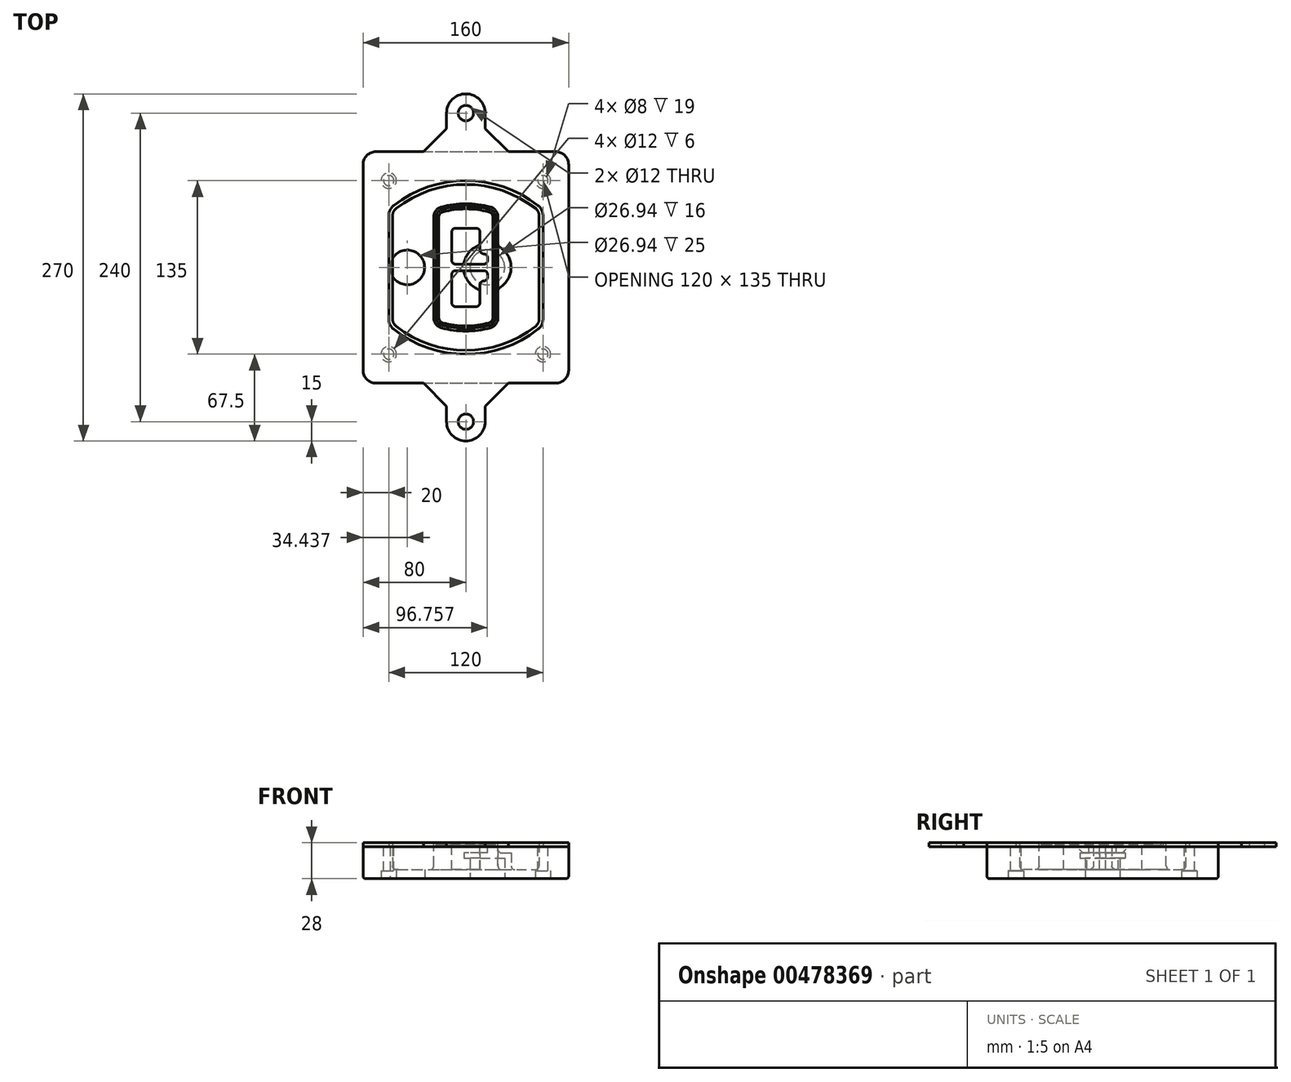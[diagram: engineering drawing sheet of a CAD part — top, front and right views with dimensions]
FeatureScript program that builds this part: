
annotation { "Feature Type Name" : "Feature", "Feature Type Description" : "" }
export const myFeature = defineFeature(function(context is Context, id is Id, definition is map)
    precondition{}
    {
        {
            var Q0;
            Q0=qCreatedBy(makeId("Top.planeOp"),FACE);
            var sketch = newSketch(context, id + "F0", { "sketchPlane" : qUnion([Q0])});
            skPoint(sketch, "E0.rect.middle", {"position": v(0, 0) * mm});
            skLineSegment(sketch, "E1.bottom", {"start": v(-70, -90) * mm, "end": v(70, -90) * mm});
            skLineSegment(sketch, "E1.top", {"start": v(-70, 90) * mm, "end": v(70, 90) * mm});
            skLineSegment(sketch, "E1.left", {"start": v(-80, -80) * mm, "end": v(-80, 80) * mm});
            skLineSegment(sketch, "E1.right", {"start": v(80, -80) * mm, "end": v(80, 80) * mm});
            skLineSegment(sketch, "E2", {"start": v(-80, 90) * mm, "end": v(80, -90) * mm, "construction": true});
            skLineSegment(sketch, "E3", {"start": v(80, 90) * mm, "end": v(-80, -90) * mm, "construction": true});
            skCircle(sketch, "E4", {"center": v(-60, 67.5) * mm, "radius": 4 * mm});
            skCircle(sketch, "E5", {"center": v(60, 67.5) * mm, "radius": 4 * mm});
            skCircle(sketch, "E6", {"center": v(60, -67.5) * mm, "radius": 4 * mm});
            skCircle(sketch, "E7", {"center": v(-60, -67.5) * mm, "radius": 4 * mm});
            skLineSegment(sketch, "E8", {"start": v(-60, 67.5) * mm, "end": v(60, 67.5) * mm, "construction": true});
            skLineSegment(sketch, "E9", {"start": v(60, 67.5) * mm, "end": v(60, -67.5) * mm, "construction": true});
            skLineSegment(sketch, "E10", {"start": v(60, -67.5) * mm, "end": v(-60, -67.5) * mm, "construction": true});
            skLineSegment(sketch, "E11", {"start": v(-60, -67.5) * mm, "end": v(-60, 67.5) * mm, "construction": true});
            skLineSegment(sketch, "E12", {"start": v(-60, 40.3) * mm, "end": v(-60, -40.3) * mm});
            skLineSegment(sketch, "E13", {"start": v(60, 40.3) * mm, "end": v(60, -40.3) * mm});
            skArc(sketch, "E14", {"start": v(56.15, 48.18) * mm, "mid": v(0, 67.5) * mm, "end": v(-56.15, 48.18) * mm});
            skArc(sketch, "E15", {"start": v(-56.15, -48.18) * mm, "mid": v(0, -67.5) * mm, "end": v(56.15, -48.18) * mm});
            skLineSegment(sketch, "E16", {"start": v(-60, 0) * mm, "end": v(60, 0) * mm, "construction": true});
            skPoint(sketch, "E17.visualSharp", {"position": v(-60, -45) * mm});
            skArc(sketch, "E17.filletArc", {"start": v(-60, -40.3) * mm, "mid": v(-58.99, -44.68) * mm, "end": v(-56.15, -48.18) * mm});
            skPoint(sketch, "E18.visualSharp", {"position": v(-60, 45) * mm});
            skArc(sketch, "E18.filletArc", {"start": v(-56.15, 48.18) * mm, "mid": v(-58.99, 44.68) * mm, "end": v(-60, 40.3) * mm});
            skPoint(sketch, "E19.visualSharp", {"position": v(60, 45) * mm});
            skArc(sketch, "E19.filletArc", {"start": v(60, 40.3) * mm, "mid": v(58.99, 44.68) * mm, "end": v(56.15, 48.18) * mm});
            skPoint(sketch, "E20.visualSharp", {"position": v(60, -45) * mm});
            skArc(sketch, "E20.filletArc", {"start": v(56.15, -48.18) * mm, "mid": v(58.99, -44.68) * mm, "end": v(60, -40.3) * mm});
            skPoint(sketch, "E21.visualSharp", {"position": v(-80, 90) * mm});
            skArc(sketch, "E21.filletArc", {"start": v(-70, 90) * mm, "mid": v(-77.07, 87.07) * mm, "end": v(-80, 80) * mm});
            skPoint(sketch, "E22.visualSharp", {"position": v(80, 90) * mm});
            skArc(sketch, "E22.filletArc", {"start": v(80, 80) * mm, "mid": v(77.07, 87.07) * mm, "end": v(70, 90) * mm});
            skPoint(sketch, "E23.visualSharp", {"position": v(80, -90) * mm});
            skArc(sketch, "E23.filletArc", {"start": v(70, -90) * mm, "mid": v(77.07, -87.07) * mm, "end": v(80, -80) * mm});
            skPoint(sketch, "E24.visualSharp", {"position": v(-80, -90) * mm});
            skArc(sketch, "E24.filletArc", {"start": v(-80, -80) * mm, "mid": v(-77.07, -87.07) * mm, "end": v(-70, -90) * mm});
            skArc(sketch, "E25.0", {"start": v(57, 40.3) * mm, "mid": v(56.3, 43.36) * mm, "end": v(54.3, 45.81) * mm});
            skLineSegment(sketch, "E25.1", {"start": v(57, 40.3) * mm, "end": v(57, -40.3) * mm});
            skArc(sketch, "E25.2", {"start": v(54.3, -45.81) * mm, "mid": v(56.3, -43.36) * mm, "end": v(57, -40.3) * mm});
            skArc(sketch, "E25.3", {"start": v(-54.3, -45.81) * mm, "mid": v(0, -64.5) * mm, "end": v(54.3, -45.81) * mm});
            skArc(sketch, "E25.4", {"start": v(-57, -40.3) * mm, "mid": v(-56.3, -43.36) * mm, "end": v(-54.3, -45.81) * mm});
            skArc(sketch, "E25.5", {"start": v(54.3, 45.81) * mm, "mid": v(0, 64.5) * mm, "end": v(-54.3, 45.81) * mm});
            skLineSegment(sketch, "E25.6", {"start": v(-57, 40.3) * mm, "end": v(-57, -40.3) * mm});
            skArc(sketch, "E25.7", {"start": v(-54.3, 45.81) * mm, "mid": v(-56.3, 43.36) * mm, "end": v(-57, 40.3) * mm});
            skArc(sketch, "E26.0", {"start": v(-58.62, 51.33) * mm, "mid": v(-62.58, 46.43) * mm, "end": v(-64, 40.3) * mm});
            skArc(sketch, "E26.1", {"start": v(58.62, 51.33) * mm, "mid": v(0, 71.5) * mm, "end": v(-58.62, 51.33) * mm});
            skArc(sketch, "E26.2", {"start": v(64, 40.3) * mm, "mid": v(62.58, 46.43) * mm, "end": v(58.62, 51.33) * mm});
            skLineSegment(sketch, "E26.3", {"start": v(64, 40.3) * mm, "end": v(64, -40.3) * mm});
            skArc(sketch, "E26.4", {"start": v(58.62, -51.33) * mm, "mid": v(62.58, -46.43) * mm, "end": v(64, -40.3) * mm});
            skLineSegment(sketch, "E26.5", {"start": v(-64, 40.3) * mm, "end": v(-64, -40.3) * mm});
            skArc(sketch, "E26.6", {"start": v(-58.62, -51.33) * mm, "mid": v(0, -71.5) * mm, "end": v(58.62, -51.33) * mm});
            skArc(sketch, "E26.7", {"start": v(-64, -40.3) * mm, "mid": v(-62.58, -46.43) * mm, "end": v(-58.62, -51.33) * mm});
            skSolve(sketch);
        }
        {
            var Q0;
            Q0=makeQuery(id+"F0.imprint","IMPRINT",FACE,{"disambiguationData":[TD([[makeQuery(id+"F0.imprint","IMPRINT",EDGE,{"derivedFrom":sQuery(id+"F0.wireOp",EDGE,"E1.bottom")}),1.0]])]});
            var Q1;
            Q1=makeQuery(id+"F0.imprint","IMPRINT",FACE,{"disambiguationData":[TD([[makeQuery(id+"F0.imprint","IMPRINT",EDGE,{"derivedFrom":sQuery(id+"F0.wireOp",EDGE,"E12")}),1.0]])]});
            var Q2;
            Q2=makeQuery(id+"F0.imprint","IMPRINT",FACE,{"disambiguationData":[TD([[makeQuery(id+"F0.imprint","IMPRINT",EDGE,{"derivedFrom":sQuery(id+"F0.wireOp",EDGE,"E25.0")}),1.0]])]});
            var Q3;
            Q3=makeQuery(id+"F0.imprint","IMPRINT",FACE,{"disambiguationData":[TD([[makeQuery(id+"F0.imprint","IMPRINT",EDGE,{"derivedFrom":sQuery(id+"F0.wireOp",EDGE,"E12")}),-1.0]])]});
            extrude(context, id + "F1", {"entities" : qUnion([Q0, Q1, Q2, Q3]), "oppositeDirection" : true, "depth" : 25 * mm});
        }
        {
            var Q0;
            Q0=makeQuery(id+"F0.imprint","IMPRINT",FACE,{"disambiguationData":[TD([[makeQuery(id+"F0.imprint","IMPRINT",EDGE,{"derivedFrom":sQuery(id+"F0.wireOp",EDGE,"E12")}),1.0]])]});
            extrude(context, id + "F2", {"entities" : qUnion([Q0]), "operationType" : NewBodyOperationType.ADD, "depth" : 3 * mm});
        }
        {
            var Q0;
            Q0=makeQuery(id+"F0.imprint","IMPRINT",FACE,{"disambiguationData":[TD([[makeQuery(id+"F0.imprint","IMPRINT",EDGE,{"derivedFrom":sQuery(id+"F0.wireOp",EDGE,"E25.0")}),1.0]])]});
            extrude(context, id + "F3", {"entities" : qUnion([Q0]), "operationType" : NewBodyOperationType.REMOVE, "oppositeDirection" : true, "depth" : 18 * mm});
        }
        {
            var Q0;
            Q0=makeQuery(id+"F2.opExtrude","CAP_FACE",FACE,{"disambiguationData":[OSD([sQuery(id+"F0.wireOp",EDGE,"E12"),sQuery(id+"F0.wireOp",EDGE,"E13"),sQuery(id+"F0.wireOp",EDGE,"E14"),sQuery(id+"F0.wireOp",EDGE,"E15"),sQuery(id+"F0.wireOp",EDGE,"E17.filletArc"),sQuery(id+"F0.wireOp",EDGE,"E18.filletArc"),sQuery(id+"F0.wireOp",EDGE,"E19.filletArc"),sQuery(id+"F0.wireOp",EDGE,"E20.filletArc"),sQuery(id+"F0.wireOp",EDGE,"E25.0"),sQuery(id+"F0.wireOp",EDGE,"E25.1"),sQuery(id+"F0.wireOp",EDGE,"E25.2"),sQuery(id+"F0.wireOp",EDGE,"E25.3"),sQuery(id+"F0.wireOp",EDGE,"E25.4"),sQuery(id+"F0.wireOp",EDGE,"E25.5"),sQuery(id+"F0.wireOp",EDGE,"E25.6"),sQuery(id+"F0.wireOp",EDGE,"E25.7")])],"isStart":false});
            var sketch = newSketch(context, id + "F4", { "sketchPlane" : qUnion([Q0])});
            skArc(sketch, "E27.0", {"start": v(-19.08, -46.97) * mm, "mid": v(0, -49.5) * mm, "end": v(19.08, -46.97) * mm});
            skArc(sketch, "E28.0", {"start": v(19.08, 46.97) * mm, "mid": v(0, 49.5) * mm, "end": v(-19.08, 46.97) * mm});
            skLineSegment(sketch, "E29", {"start": v(-25, 39.25) * mm, "end": v(-25, -39.25) * mm});
            skLineSegment(sketch, "E30", {"start": v(25, 39.25) * mm, "end": v(25, -39.25) * mm});
            skLineSegment(sketch, "E31", {"start": v(-25, 45.1) * mm, "end": v(25, 45.1) * mm, "construction": true});
            skLineSegment(sketch, "E32", {"start": v(-25, -45.1) * mm, "end": v(25, -45.1) * mm, "construction": true});
            skPoint(sketch, "E33.visualSharp", {"position": v(-25, 45.1) * mm});
            skArc(sketch, "E33.filletArc", {"start": v(-19.08, 46.97) * mm, "mid": v(-23.35, 44.11) * mm, "end": v(-25, 39.25) * mm});
            skPoint(sketch, "E34.visualSharp", {"position": v(25, 45.1) * mm});
            skArc(sketch, "E34.filletArc", {"start": v(25, 39.25) * mm, "mid": v(23.35, 44.11) * mm, "end": v(19.08, 46.97) * mm});
            skPoint(sketch, "E35.visualSharp", {"position": v(25, -45.1) * mm});
            skArc(sketch, "E35.filletArc", {"start": v(19.08, -46.97) * mm, "mid": v(23.35, -44.11) * mm, "end": v(25, -39.25) * mm});
            skPoint(sketch, "E36.visualSharp", {"position": v(-25, -45.1) * mm});
            skArc(sketch, "E36.filletArc", {"start": v(-25, -39.25) * mm, "mid": v(-23.35, -44.11) * mm, "end": v(-19.08, -46.97) * mm});
            skArc(sketch, "E37.0", {"start": v(54.3, 45.81) * mm, "mid": v(0, 64.5) * mm, "end": v(-54.3, 45.81) * mm});
            skArc(sketch, "E37.1", {"start": v(-54.3, 45.81) * mm, "mid": v(-56.3, 43.36) * mm, "end": v(-57, 40.3) * mm});
            skLineSegment(sketch, "E37.2", {"start": v(-57, 40.3) * mm, "end": v(-57, -40.3) * mm});
            skArc(sketch, "E37.3", {"start": v(-57, -40.3) * mm, "mid": v(-56.3, -43.36) * mm, "end": v(-54.3, -45.81) * mm});
            skArc(sketch, "E37.4", {"start": v(-54.3, -45.81) * mm, "mid": v(0, -64.5) * mm, "end": v(54.3, -45.81) * mm});
            skArc(sketch, "E37.5", {"start": v(54.3, -45.81) * mm, "mid": v(56.3, -43.36) * mm, "end": v(57, -40.3) * mm});
            skLineSegment(sketch, "E37.6", {"start": v(57, 40.3) * mm, "end": v(57, -40.3) * mm});
            skArc(sketch, "E37.7", {"start": v(57, 40.3) * mm, "mid": v(56.3, 43.36) * mm, "end": v(54.3, 45.81) * mm});
            skLineSegment(sketch, "E38.0", {"start": v(23, 39.25) * mm, "end": v(23, -39.25) * mm});
            skArc(sketch, "E38.1", {"start": v(18.56, -45.04) * mm, "mid": v(21.76, -42.9) * mm, "end": v(23, -39.25) * mm});
            skArc(sketch, "E38.2", {"start": v(-18.56, -45.04) * mm, "mid": v(0, -47.5) * mm, "end": v(18.56, -45.04) * mm});
            skArc(sketch, "E38.3", {"start": v(-23, -39.25) * mm, "mid": v(-21.76, -42.9) * mm, "end": v(-18.56, -45.04) * mm});
            skLineSegment(sketch, "E38.4", {"start": v(-23, 39.25) * mm, "end": v(-23, -39.25) * mm});
            skArc(sketch, "E38.5", {"start": v(23, 39.25) * mm, "mid": v(21.76, 42.9) * mm, "end": v(18.56, 45.04) * mm});
            skArc(sketch, "E38.6", {"start": v(-18.56, 45.04) * mm, "mid": v(-21.76, 42.9) * mm, "end": v(-23, 39.25) * mm});
            skArc(sketch, "E38.7", {"start": v(18.56, 45.04) * mm, "mid": v(0, 47.5) * mm, "end": v(-18.56, 45.04) * mm});
            skArc(sketch, "E39.0", {"start": v(21, 39.25) * mm, "mid": v(20.18, 41.68) * mm, "end": v(18.04, 43.1) * mm});
            skLineSegment(sketch, "E39.1", {"start": v(21, 39.25) * mm, "end": v(21, -39.25) * mm});
            skArc(sketch, "E39.2", {"start": v(18.04, -43.1) * mm, "mid": v(20.18, -41.68) * mm, "end": v(21, -39.25) * mm});
            skArc(sketch, "E39.3", {"start": v(-18.04, -43.1) * mm, "mid": v(0, -45.5) * mm, "end": v(18.04, -43.1) * mm});
            skArc(sketch, "E39.4", {"start": v(-21, -39.25) * mm, "mid": v(-20.18, -41.68) * mm, "end": v(-18.04, -43.1) * mm});
            skArc(sketch, "E39.5", {"start": v(18.04, 43.1) * mm, "mid": v(0, 45.5) * mm, "end": v(-18.04, 43.1) * mm});
            skLineSegment(sketch, "E39.6", {"start": v(-21, 39.25) * mm, "end": v(-21, -39.25) * mm});
            skArc(sketch, "E39.7", {"start": v(-18.04, 43.1) * mm, "mid": v(-20.18, 41.68) * mm, "end": v(-21, 39.25) * mm});
            skLineSegment(sketch, "E40", {"start": v(-25, 0) * mm, "end": v(25, 0) * mm, "construction": true});
            skLineSegment(sketch, "E41", {"start": v(-11, 5.5) * mm, "end": v(-11, 27.5) * mm});
            skLineSegment(sketch, "E42", {"start": v(-8, 30.5) * mm, "end": v(8, 30.5) * mm});
            skLineSegment(sketch, "E43", {"start": v(11, 27.5) * mm, "end": v(11, 13.5) * mm});
            skLineSegment(sketch, "E44", {"start": v(14, 10.5) * mm, "end": v(14, 10.5) * mm});
            skLineSegment(sketch, "E45", {"start": v(17, 7.5) * mm, "end": v(17, 5.5) * mm});
            skLineSegment(sketch, "E46", {"start": v(14, 2.5) * mm, "end": v(-8, 2.5) * mm});
            skPoint(sketch, "E47.visualSharp", {"position": v(-11, 30.5) * mm});
            skArc(sketch, "E47.filletArc", {"start": v(-8, 30.5) * mm, "mid": v(-10.12, 29.62) * mm, "end": v(-11, 27.5) * mm});
            skPoint(sketch, "E48.visualSharp", {"position": v(11, 30.5) * mm});
            skArc(sketch, "E48.filletArc", {"start": v(11, 27.5) * mm, "mid": v(10.12, 29.62) * mm, "end": v(8, 30.5) * mm});
            skPoint(sketch, "E49.visualSharp", {"position": v(11, 10.5) * mm});
            skArc(sketch, "E49.filletArc", {"start": v(11, 13.5) * mm, "mid": v(11.88, 11.38) * mm, "end": v(14, 10.5) * mm});
            skPoint(sketch, "E50.visualSharp", {"position": v(17, 10.5) * mm});
            skArc(sketch, "E50.filletArc", {"start": v(17, 7.5) * mm, "mid": v(16.12, 9.62) * mm, "end": v(14, 10.5) * mm});
            skPoint(sketch, "E51.visualSharp", {"position": v(17, 2.5) * mm});
            skArc(sketch, "E51.filletArc", {"start": v(14, 2.5) * mm, "mid": v(16.12, 3.38) * mm, "end": v(17, 5.5) * mm});
            skPoint(sketch, "E52.visualSharp", {"position": v(-11, 2.5) * mm});
            skArc(sketch, "E52.filletArc", {"start": v(-11, 5.5) * mm, "mid": v(-10.12, 3.38) * mm, "end": v(-8, 2.5) * mm});
            skLineSegment(sketch, "E53.0.MirrorCS", {"start": v(14, -2.5) * mm, "end": v(-8, -2.5) * mm});
            skArc(sketch, "E54.0.MirrorCS", {"start": v(-11, -5.5) * mm, "mid": v(-10.12, -3.38) * mm, "end": v(-8, -2.5) * mm});
            skLineSegment(sketch, "E55.0.MirrorCS", {"start": v(-11, -5.5) * mm, "end": v(-11, -27.5) * mm});
            skArc(sketch, "E56.0.MirrorCS", {"start": v(-8, -30.5) * mm, "mid": v(-10.12, -29.62) * mm, "end": v(-11, -27.5) * mm});
            skLineSegment(sketch, "E57.0.MirrorCS", {"start": v(-8, -30.5) * mm, "end": v(8, -30.5) * mm});
            skArc(sketch, "E58.0.MirrorCS", {"start": v(11, -27.5) * mm, "mid": v(10.12, -29.62) * mm, "end": v(8, -30.5) * mm});
            skLineSegment(sketch, "E59.0.MirrorCS", {"start": v(11, -27.5) * mm, "end": v(11, -13.5) * mm});
            skArc(sketch, "E60.0.MirrorCS", {"start": v(11, -13.5) * mm, "mid": v(11.88, -11.38) * mm, "end": v(14, -10.5) * mm});
            skArc(sketch, "E61.0.MirrorCS", {"start": v(17, -7.5) * mm, "mid": v(16.12, -9.62) * mm, "end": v(14, -10.5) * mm});
            skLineSegment(sketch, "E62.0.MirrorCS", {"start": v(17, -7.5) * mm, "end": v(17, -5.5) * mm});
            skArc(sketch, "E63.0.MirrorCS", {"start": v(14, -2.5) * mm, "mid": v(16.12, -3.38) * mm, "end": v(17, -5.5) * mm});
            skSolve(sketch);
        }
        {
            var Q0;
            Q0=makeQuery(id+"F4.imprint","IMPRINT",FACE,{"disambiguationData":[TD([[makeQuery(id+"F4.imprint","IMPRINT",EDGE,{"derivedFrom":sQuery(id+"F4.wireOp",EDGE,"E27.0")}),1.0]])]});
            var Q1;
            Q1=makeQuery(id+"F4.imprint","IMPRINT",FACE,{"disambiguationData":[TD([[makeQuery(id+"F4.imprint","IMPRINT",EDGE,{"derivedFrom":sQuery(id+"F4.wireOp",EDGE,"E38.0")}),-1.0]])]});
            var Q2;
            Q2=makeQuery(id+"F4.imprint","IMPRINT",FACE,{"disambiguationData":[TD([[makeQuery(id+"F4.imprint","IMPRINT",EDGE,{"derivedFrom":sQuery(id+"F4.wireOp",EDGE,"E39.0")}),1.0]])]});
            extrude(context, id + "F5", {"entities" : qUnion([Q0, Q1, Q2]), "operationType" : NewBodyOperationType.ADD, "endBound" : BoundingType.UP_TO_NEXT, "oppositeDirection" : true, "depth" : 25 * mm});
        }
        {
            var Q0;
            Q0=makeQuery(id+"F4.imprint","IMPRINT",FACE,{"disambiguationData":[TD([[makeQuery(id+"F4.imprint","IMPRINT",EDGE,{"derivedFrom":sQuery(id+"F4.wireOp",EDGE,"E38.0")}),-1.0]])]});
            extrude(context, id + "F6", {"entities" : qUnion([Q0]), "operationType" : NewBodyOperationType.REMOVE, "oppositeDirection" : true, "depth" : 2 * mm});
        }
        {
            var Q0;
            Q0=makeQuery(id+"F1.opExtrude","CAP_FACE",FACE,{"disambiguationData":[OSD([sQuery(id+"F0.wireOp",EDGE,"E1.bottom"),sQuery(id+"F0.wireOp",EDGE,"E1.top"),sQuery(id+"F0.wireOp",EDGE,"E1.left"),sQuery(id+"F0.wireOp",EDGE,"E1.right"),sQuery(id+"F0.wireOp",EDGE,"E4"),sQuery(id+"F0.wireOp",EDGE,"E5"),sQuery(id+"F0.wireOp",EDGE,"E6"),sQuery(id+"F0.wireOp",EDGE,"E7"),sQuery(id+"F0.wireOp",EDGE,"E21.filletArc"),sQuery(id+"F0.wireOp",EDGE,"E22.filletArc"),sQuery(id+"F0.wireOp",EDGE,"E23.filletArc"),sQuery(id+"F0.wireOp",EDGE,"E24.filletArc")])],"isStart":false});
            var sketch = newSketch(context, id + "F7", { "sketchPlane" : qUnion([Q0])});
            skCircle(sketch, "E64", {"center": v(16.76, 0) * mm, "radius": 13.47 * mm});
            skCircle(sketch, "E65", {"center": v(-45.56, 0) * mm, "radius": 13.47 * mm});
            skLineSegment(sketch, "E66", {"start": v(80, 0) * mm, "end": v(-80, 0) * mm});
            skCircle(sketch, "E67", {"center": v(16.76, 0) * mm, "radius": 18.47 * mm});
            skCircle(sketch, "E68", {"center": v(60, -67.5) * mm, "radius": 6 * mm});
            skCircle(sketch, "E69", {"center": v(-60, -67.5) * mm, "radius": 6 * mm});
            skCircle(sketch, "E70", {"center": v(-60, 67.5) * mm, "radius": 6 * mm});
            skCircle(sketch, "E71", {"center": v(60, 67.5) * mm, "radius": 6 * mm});
            skSolve(sketch);
        }
        {
            var Q0;
            {var subQ1=sQuery(id+"F7.wireOp",EDGE,"E66");var subQ4=sQuery(id+"F7.wireOp",EDGE,"E64");var subQ6=makeQuery(id+"F7.imprint","INTERSECT",VERTEX,{"disambiguationData":[OD(0.0)],"derivedFrom":[subQ4,subQ1]});Q0=makeQuery(id+"F7.imprint","IMPRINT",FACE,{"disambiguationData":[TD([[makeQuery(id+"F7.imprint","IMPRINT",EDGE,{"disambiguationData":[TD([[subQ6,-1.0]])],"derivedFrom":subQ4}),-1.0]])]});}
            var Q1;
            {var subQ0=sQuery(id+"F7.wireOp",EDGE,"E66");var subQ1=sQuery(id+"F7.wireOp",EDGE,"E64");var subQ3=makeQuery(id+"F7.imprint","INTERSECT",VERTEX,{"disambiguationData":[OD(0.0)],"derivedFrom":[subQ1,subQ0]});Q1=makeQuery(id+"F7.imprint","IMPRINT",FACE,{"disambiguationData":[TD([[makeQuery(id+"F7.imprint","IMPRINT",EDGE,{"disambiguationData":[TD([[subQ3,-1.0]])],"derivedFrom":subQ1}),1.0]])]});}
            var Q2;
            {var subQ0=sQuery(id+"F7.wireOp",EDGE,"E66");var subQ1=sQuery(id+"F7.wireOp",EDGE,"E64");var subQ3=makeQuery(id+"F7.imprint","INTERSECT",VERTEX,{"disambiguationData":[OD(0.0)],"derivedFrom":[subQ1,subQ0]});Q2=makeQuery(id+"F7.imprint","IMPRINT",FACE,{"disambiguationData":[TD([[makeQuery(id+"F7.imprint","IMPRINT",EDGE,{"disambiguationData":[TD([[subQ3,1.0]])],"derivedFrom":subQ1}),1.0]])]});}
            var Q3;
            {var subQ1=sQuery(id+"F7.wireOp",EDGE,"E66");var subQ4=sQuery(id+"F7.wireOp",EDGE,"E64");var subQ6=makeQuery(id+"F7.imprint","INTERSECT",VERTEX,{"disambiguationData":[OD(0.0)],"derivedFrom":[subQ4,subQ1]});Q3=makeQuery(id+"F7.imprint","IMPRINT",FACE,{"disambiguationData":[TD([[makeQuery(id+"F7.imprint","IMPRINT",EDGE,{"disambiguationData":[TD([[subQ6,1.0]])],"derivedFrom":subQ4}),-1.0]])]});}
            extrude(context, id + "F8", {"entities" : qUnion([Q0, Q1, Q2, Q3]), "operationType" : NewBodyOperationType.ADD, "oppositeDirection" : true, "depth" : 20 * mm});
        }
        {
            var Q0;
            {var subQ0=sQuery(id+"F7.wireOp",EDGE,"E66");var subQ1=sQuery(id+"F7.wireOp",EDGE,"E64");var subQ3=makeQuery(id+"F7.imprint","INTERSECT",VERTEX,{"disambiguationData":[OD(0.0)],"derivedFrom":[subQ1,subQ0]});Q0=makeQuery(id+"F7.imprint","IMPRINT",FACE,{"disambiguationData":[TD([[makeQuery(id+"F7.imprint","IMPRINT",EDGE,{"disambiguationData":[TD([[subQ3,-1.0]])],"derivedFrom":subQ1}),1.0]])]});}
            var Q1;
            {var subQ0=sQuery(id+"F7.wireOp",EDGE,"E66");var subQ1=sQuery(id+"F7.wireOp",EDGE,"E64");var subQ3=makeQuery(id+"F7.imprint","INTERSECT",VERTEX,{"disambiguationData":[OD(0.0)],"derivedFrom":[subQ1,subQ0]});Q1=makeQuery(id+"F7.imprint","IMPRINT",FACE,{"disambiguationData":[TD([[makeQuery(id+"F7.imprint","IMPRINT",EDGE,{"disambiguationData":[TD([[subQ3,1.0]])],"derivedFrom":subQ1}),1.0]])]});}
            extrude(context, id + "F9", {"entities" : qUnion([Q0, Q1]), "operationType" : NewBodyOperationType.REMOVE, "oppositeDirection" : true, "depth" : 16 * mm});
        }
        {
            var Q0;
            {var subQ0=sQuery(id+"F7.wireOp",EDGE,"E66");var subQ1=sQuery(id+"F7.wireOp",EDGE,"E65");var subQ3=makeQuery(id+"F7.imprint","INTERSECT",VERTEX,{"disambiguationData":[OD(0.0)],"derivedFrom":[subQ1,subQ0]});Q0=makeQuery(id+"F7.imprint","IMPRINT",FACE,{"disambiguationData":[TD([[makeQuery(id+"F7.imprint","IMPRINT",EDGE,{"disambiguationData":[TD([[subQ3,-1.0]])],"derivedFrom":subQ1}),1.0]])]});}
            var Q1;
            {var subQ0=sQuery(id+"F7.wireOp",EDGE,"E66");var subQ1=sQuery(id+"F7.wireOp",EDGE,"E65");var subQ3=makeQuery(id+"F7.imprint","INTERSECT",VERTEX,{"disambiguationData":[OD(0.0)],"derivedFrom":[subQ1,subQ0]});Q1=makeQuery(id+"F7.imprint","IMPRINT",FACE,{"disambiguationData":[TD([[makeQuery(id+"F7.imprint","IMPRINT",EDGE,{"disambiguationData":[TD([[subQ3,1.0]])],"derivedFrom":subQ1}),1.0]])]});}
            extrude(context, id + "F10", {"entities" : qUnion([Q0, Q1]), "operationType" : NewBodyOperationType.REMOVE, "oppositeDirection" : true, "depth" : 25 * mm});
        }
        {
            var Q0;
            Q0=makeQuery(id+"F7.imprint","IMPRINT",FACE,{"disambiguationData":[TD([[makeQuery(id+"F7.imprint","IMPRINT",EDGE,{"derivedFrom":sQuery(id+"F7.wireOp",EDGE,"E68")}),1.0]])]});
            var Q1;
            Q1=makeQuery(id+"F7.imprint","IMPRINT",FACE,{"disambiguationData":[TD([[makeQuery(id+"F7.imprint","IMPRINT",EDGE,{"derivedFrom":makeQuery(id+"F1.opExtrude","CAP_EDGE",EDGE,{"disambiguationData":[OSD([sQuery(id+"F0.wireOp",EDGE,"E5")])],"isStart":false})}),-1.0]])]});
            var Q2;
            Q2=makeQuery(id+"F7.imprint","IMPRINT",FACE,{"disambiguationData":[TD([[makeQuery(id+"F7.imprint","IMPRINT",EDGE,{"derivedFrom":sQuery(id+"F7.wireOp",EDGE,"E69")}),1.0]])]});
            var Q3;
            Q3=makeQuery(id+"F7.imprint","IMPRINT",FACE,{"disambiguationData":[TD([[makeQuery(id+"F7.imprint","IMPRINT",EDGE,{"derivedFrom":makeQuery(id+"F1.opExtrude","CAP_EDGE",EDGE,{"disambiguationData":[OSD([sQuery(id+"F0.wireOp",EDGE,"E4")])],"isStart":false})}),-1.0]])]});
            var Q4;
            Q4=makeQuery(id+"F7.imprint","IMPRINT",FACE,{"disambiguationData":[TD([[makeQuery(id+"F7.imprint","IMPRINT",EDGE,{"derivedFrom":sQuery(id+"F7.wireOp",EDGE,"E70")}),1.0]])]});
            var Q5;
            Q5=makeQuery(id+"F7.imprint","IMPRINT",FACE,{"disambiguationData":[TD([[makeQuery(id+"F7.imprint","IMPRINT",EDGE,{"derivedFrom":makeQuery(id+"F1.opExtrude","CAP_EDGE",EDGE,{"disambiguationData":[OSD([sQuery(id+"F0.wireOp",EDGE,"E7")])],"isStart":false})}),-1.0]])]});
            var Q6;
            Q6=makeQuery(id+"F7.imprint","IMPRINT",FACE,{"disambiguationData":[TD([[makeQuery(id+"F7.imprint","IMPRINT",EDGE,{"derivedFrom":sQuery(id+"F7.wireOp",EDGE,"E71")}),1.0]])]});
            var Q7;
            Q7=makeQuery(id+"F7.imprint","IMPRINT",FACE,{"disambiguationData":[TD([[makeQuery(id+"F7.imprint","IMPRINT",EDGE,{"derivedFrom":makeQuery(id+"F1.opExtrude","CAP_EDGE",EDGE,{"disambiguationData":[OSD([sQuery(id+"F0.wireOp",EDGE,"E6")])],"isStart":false})}),-1.0]])]});
            extrude(context, id + "F11", {"entities" : qUnion([Q0, Q1, Q2, Q3, Q4, Q5, Q6, Q7]), "operationType" : NewBodyOperationType.REMOVE, "oppositeDirection" : true, "depth" : 6 * mm});
        }
        {
            var Q0;
            Q0=makeQuery(id+"F9.boolean.opBoolean","COPY",FACE,{"derivedFrom":makeQuery(id+"F9.opExtrude","CAP_FACE",FACE,{"disambiguationData":[OSD([sQuery(id+"F7.wireOp",EDGE,"E64")])],"isStart":false})});
            var sketch = newSketch(context, id + "F12", { "sketchPlane" : qUnion([Q0])});
            skArc(sketch, "E72.0", {"start": v(11, 17.55) * mm, "mid": v(2.57, 11.82) * mm, "end": v(-1.54, 2.5) * mm});
            skArc(sketch, "E72.1", {"start": v(-1.54, -2.5) * mm, "mid": v(2.57, -11.82) * mm, "end": v(11, -17.55) * mm});
            skLineSegment(sketch, "E73", {"start": v(-1.54, -2.5) * mm, "end": v(14, -2.5) * mm});
            skLineSegment(sketch, "E74.0", {"start": v(14, 2.5) * mm, "end": v(-1.54, 2.5) * mm});
            skArc(sketch, "E74.1", {"start": v(14, 2.5) * mm, "mid": v(16.12, 3.38) * mm, "end": v(17, 5.5) * mm});
            skLineSegment(sketch, "E74.2", {"start": v(17, 7.5) * mm, "end": v(17, 5.5) * mm});
            skArc(sketch, "E74.3", {"start": v(17, 7.5) * mm, "mid": v(16.12, 9.62) * mm, "end": v(14, 10.5) * mm});
            skArc(sketch, "E74.4", {"start": v(11, 13.5) * mm, "mid": v(11.88, 11.38) * mm, "end": v(14, 10.5) * mm});
            skLineSegment(sketch, "E74.5", {"start": v(11, 17.55) * mm, "end": v(11, 13.5) * mm});
            skLineSegment(sketch, "E74.7", {"start": v(14, -2.5) * mm, "end": v(-1.54, -2.5) * mm});
            skArc(sketch, "E74.8", {"start": v(14, -2.5) * mm, "mid": v(16.12, -3.38) * mm, "end": v(17, -5.5) * mm});
            skLineSegment(sketch, "E74.9", {"start": v(17, -7.5) * mm, "end": v(17, -5.5) * mm});
            skArc(sketch, "E74.10", {"start": v(17, -7.5) * mm, "mid": v(16.12, -9.62) * mm, "end": v(14, -10.5) * mm});
            skArc(sketch, "E74.11", {"start": v(11, -13.5) * mm, "mid": v(11.88, -11.38) * mm, "end": v(14, -10.5) * mm});
            skLineSegment(sketch, "E74.12", {"start": v(11, -17.55) * mm, "end": v(11, -13.5) * mm});
            skPoint(sketch, "E75.orphan", {"position": v(11, -27.5) * mm});
            skPoint(sketch, "E76.orphan", {"position": v(-8, -2.5) * mm});
            skPoint(sketch, "E77.orphan", {"position": v(-8, 2.5) * mm});
            skPoint(sketch, "E78.orphan", {"position": v(11, 27.5) * mm});
            skSolve(sketch);
        }
        {
            var Q0;
            {var subQ7=sQuery(id+"F12.wireOp",EDGE,"E72.0");var subQ14=sQuery(id+"F12.wireOp",EDGE,"E72.1");var subQ16=sQuery(id+"F12.wireOp",EDGE,"E74.1");var subQ18=sQuery(id+"F12.wireOp",EDGE,"E74.8");Q0=qUnion([makeQuery(id+"F12.imprint","IMPRINT",FACE,{"disambiguationData":[TD([[makeQuery(id+"F12.imprint","IMPRINT",EDGE,{"derivedFrom":subQ7}),1.0]])]}),makeQuery(id+"F12.imprint","IMPRINT",FACE,{"disambiguationData":[TD([[makeQuery(id+"F12.imprint","IMPRINT",EDGE,{"derivedFrom":subQ14}),1.0]])]}),makeQuery(id+"F12.imprint","IMPRINT",FACE,{"disambiguationData":[TD([[makeQuery(id+"F12.imprint","IMPRINT",EDGE,{"derivedFrom":subQ16}),1.0]])]}),makeQuery(id+"F12.imprint","IMPRINT",FACE,{"disambiguationData":[TD([[makeQuery(id+"F12.imprint","IMPRINT",EDGE,{"derivedFrom":subQ18}),-1.0]])]})]);}
            var Q1;
            Q1=makeQuery(id+"F5.boolean.opBoolean","SPLIT",FACE,{"disambiguationData":[TD([makeQuery(id+"F5.opExtrude","SWEPT_FACE",FACE,{"disambiguationData":[OSD([sQuery(id+"F4.wireOp",EDGE,"E41")])]})])],"derivedFrom":makeQuery(id+"F3.boolean.opBoolean","COPY",FACE,{"derivedFrom":makeQuery(id+"F3.opExtrude","CAP_FACE",FACE,{"disambiguationData":[OSD([sQuery(id+"F0.wireOp",EDGE,"E25.0"),sQuery(id+"F0.wireOp",EDGE,"E25.1"),sQuery(id+"F0.wireOp",EDGE,"E25.2"),sQuery(id+"F0.wireOp",EDGE,"E25.3"),sQuery(id+"F0.wireOp",EDGE,"E25.4"),sQuery(id+"F0.wireOp",EDGE,"E25.5"),sQuery(id+"F0.wireOp",EDGE,"E25.6"),sQuery(id+"F0.wireOp",EDGE,"E25.7")])],"isStart":false})})});
            extrude(context, id + "F13", {"entities" : qUnion([Q0]), "operationType" : NewBodyOperationType.REMOVE, "endBound" : BoundingType.UP_TO_SURFACE, "endBoundEntityFace" : qUnion([Q1]), "depth" : 25 * mm});
        }
        {
            var Q0;
            Q0=makeQuery(id+"F3.boolean.opBoolean","COPY",EDGE,{"derivedFrom":makeQuery(id+"F3.opExtrude","CAP_EDGE",EDGE,{"disambiguationData":[OSD([sQuery(id+"F0.wireOp",EDGE,"E25.6")])],"isStart":false})});
            var Q1;
            Q1=makeQuery(id+"F8.boolean.opBoolean","INTERSECT",EDGE,{"derivedFrom":[makeQuery(id+"F5.opExtrude","SWEPT_FACE",FACE,{"disambiguationData":[OSD([sQuery(id+"F4.wireOp",EDGE,"E30")])]}),makeQuery(id+"F8.opExtrude","CAP_FACE",FACE,{"disambiguationData":[OSD([sQuery(id+"F7.wireOp",EDGE,"E67")])],"isStart":false})]});
            var Q2;
            Q2=makeQuery(id+"F8.boolean.opBoolean","INTERSECT",EDGE,{"disambiguationData":[OD(1.0)],"derivedFrom":[makeQuery(id+"F5.opExtrude","SWEPT_FACE",FACE,{"disambiguationData":[OSD([sQuery(id+"F4.wireOp",EDGE,"E30")])]}),makeQuery(id+"F8.opExtrude","SWEPT_FACE",FACE,{"disambiguationData":[OSD([sQuery(id+"F7.wireOp",EDGE,"E67")])]})]});
            var Q3;
            {var subQ0=sQuery(id+"F4.wireOp",EDGE,"E30");Q3=makeQuery(id+"F8.boolean.opBoolean","SPLIT",EDGE,{"disambiguationData":[TD([makeQuery(id+"F5.opExtrude","SWEPT_FACE",FACE,{"disambiguationData":[OSD([sQuery(id+"F4.wireOp",EDGE,"E35.filletArc")])]})])],"derivedFrom":makeQuery(id+"F5.opExtrude","CAP_EDGE",EDGE,{"disambiguationData":[OSD([subQ0])],"isStart":false})});}
            var Q4;
            {var subQ0=sQuery(id+"F0.wireOp",EDGE,"E25.7");var subQ1=sQuery(id+"F0.wireOp",EDGE,"E25.1");var subQ2=sQuery(id+"F0.wireOp",EDGE,"E25.6");var subQ3=sQuery(id+"F0.wireOp",EDGE,"E25.5");var subQ4=sQuery(id+"F0.wireOp",EDGE,"E25.4");var subQ5=sQuery(id+"F0.wireOp",EDGE,"E25.0");var subQ6=sQuery(id+"F0.wireOp",EDGE,"E25.2");var subQ7=sQuery(id+"F0.wireOp",EDGE,"E25.3");Q4=makeQuery(id+"F8.boolean.opBoolean","INTERSECT",EDGE,{"derivedFrom":[makeQuery(id+"F5.boolean.opBoolean","SPLIT",FACE,{"disambiguationData":[TD([makeQuery(id+"F2.opExtrude","SWEPT_FACE",FACE,{"disambiguationData":[OSD([subQ5])]})])],"derivedFrom":makeQuery(id+"F3.boolean.opBoolean","COPY",FACE,{"derivedFrom":makeQuery(id+"F3.opExtrude","CAP_FACE",FACE,{"disambiguationData":[OSD([subQ5,subQ1,subQ6,subQ7,subQ4,subQ3,subQ2,subQ0])],"isStart":false})})}),makeQuery(id+"F8.opExtrude","SWEPT_FACE",FACE,{"disambiguationData":[OSD([sQuery(id+"F7.wireOp",EDGE,"E67")])]})]});}
            var Q5;
            Q5=makeQuery(id+"F8.boolean.opBoolean","INTERSECT",EDGE,{"disambiguationData":[OD(0.0)],"derivedFrom":[makeQuery(id+"F5.opExtrude","SWEPT_FACE",FACE,{"disambiguationData":[OSD([sQuery(id+"F4.wireOp",EDGE,"E30")])]}),makeQuery(id+"F8.opExtrude","SWEPT_FACE",FACE,{"disambiguationData":[OSD([sQuery(id+"F7.wireOp",EDGE,"E67")])]})]});
            fillet(context, id + "F14", {"entities" : qUnion([Q0, Q1, Q2, Q3, Q4, Q5]), "radius" : 3 * mm, "tangentPropagation" : true, "allowEdgeOverflow" : false});
        }
        {
            var Q0;
            Q0=makeQuery(id+"F1.opExtrude","CAP_EDGE",EDGE,{"disambiguationData":[OSD([sQuery(id+"F0.wireOp",EDGE,"E1.bottom")])],"isStart":false});
            fillet(context, id + "F15", {"entities" : qUnion([Q0]), "radius" : 2 * mm, "tangentPropagation" : true, "allowEdgeOverflow" : false});
        }
        {
            var Q0;
            {var subQ0=sQuery(id+"F0.wireOp",EDGE,"E21.filletArc");var subQ1=sQuery(id+"F0.wireOp",EDGE,"E7");var subQ2=sQuery(id+"F0.wireOp",EDGE,"E6");var subQ3=sQuery(id+"F0.wireOp",EDGE,"E5");var subQ4=sQuery(id+"F0.wireOp",EDGE,"E4");var subQ5=sQuery(id+"F0.wireOp",EDGE,"E22.filletArc");var subQ6=sQuery(id+"F0.wireOp",EDGE,"E1.bottom");var subQ7=sQuery(id+"F0.wireOp",EDGE,"E1.right");var subQ8=sQuery(id+"F0.wireOp",EDGE,"E1.top");var subQ9=sQuery(id+"F0.wireOp",EDGE,"E1.left");var subQ10=sQuery(id+"F0.wireOp",EDGE,"E23.filletArc");var subQ11=sQuery(id+"F0.wireOp",EDGE,"E24.filletArc");Q0=makeQuery(id+"F2.boolean.opBoolean","SPLIT",FACE,{"disambiguationData":[TD([makeQuery(id+"F1.opExtrude","SWEPT_FACE",FACE,{"disambiguationData":[OSD([subQ6])]})])],"derivedFrom":makeQuery(id+"F1.opExtrude","CAP_FACE",FACE,{"disambiguationData":[OSD([subQ6,subQ8,subQ9,subQ7,subQ4,subQ3,subQ2,subQ1,subQ0,subQ5,subQ10,subQ11])],"isStart":true})});}
            var sketch = newSketch(context, id + "F16", { "sketchPlane" : qUnion([Q0])});
            skLineSegment(sketch, "E79.0", {"start": v(60, 40.3) * mm, "end": v(60, -40.3) * mm});
            skArc(sketch, "E79.1", {"start": v(60, 40.3) * mm, "mid": v(58.99, 44.68) * mm, "end": v(56.15, 48.18) * mm});
            skArc(sketch, "E79.2", {"start": v(56.15, 48.18) * mm, "mid": v(0, 67.5) * mm, "end": v(-56.15, 48.18) * mm});
            skArc(sketch, "E79.3", {"start": v(-56.15, 48.18) * mm, "mid": v(-58.99, 44.68) * mm, "end": v(-60, 40.3) * mm});
            skLineSegment(sketch, "E79.4", {"start": v(-60, 40.3) * mm, "end": v(-60, -40.3) * mm});
            skArc(sketch, "E79.5", {"start": v(-60, -40.3) * mm, "mid": v(-58.99, -44.68) * mm, "end": v(-56.15, -48.18) * mm});
            skArc(sketch, "E79.6", {"start": v(-56.15, -48.18) * mm, "mid": v(0, -67.5) * mm, "end": v(56.15, -48.18) * mm});
            skArc(sketch, "E79.7", {"start": v(56.15, -48.18) * mm, "mid": v(58.99, -44.68) * mm, "end": v(60, -40.3) * mm});
            skLineSegment(sketch, "E79.8", {"start": v(80, -80) * mm, "end": v(80, 80) * mm});
            skArc(sketch, "E79.9", {"start": v(80, 80) * mm, "mid": v(77.07, 87.07) * mm, "end": v(70, 90) * mm});
            skLineSegment(sketch, "E79.10", {"start": v(-70, 90) * mm, "end": v(70, 90) * mm});
            skArc(sketch, "E79.11", {"start": v(-70, 90) * mm, "mid": v(-77.07, 87.07) * mm, "end": v(-80, 80) * mm});
            skLineSegment(sketch, "E79.12", {"start": v(-80, -80) * mm, "end": v(-80, 80) * mm});
            skArc(sketch, "E79.13", {"start": v(-80, -80) * mm, "mid": v(-77.07, -87.07) * mm, "end": v(-70, -90) * mm});
            skLineSegment(sketch, "E79.14", {"start": v(-70, -90) * mm, "end": v(70, -90) * mm});
            skArc(sketch, "E79.15", {"start": v(70, -90) * mm, "mid": v(77.07, -87.07) * mm, "end": v(80, -80) * mm});
            skLineSegment(sketch, "E80", {"start": v(0, 90) * mm, "end": v(0, 120) * mm, "construction": true});
            skPoint(sketch, "E80.endSnap0", {"position": v(0, 90) * mm});
            skCircle(sketch, "E81", {"center": v(0, 120) * mm, "radius": 6 * mm});
            skLineSegment(sketch, "E82", {"start": v(-33, 90) * mm, "end": v(-15, 108) * mm});
            skLineSegment(sketch, "E83", {"start": v(-15, 108) * mm, "end": v(-15, 120) * mm});
            skArc(sketch, "E84", {"start": v(-15, 120) * mm, "mid": v(0, 135) * mm, "end": v(15, 120) * mm});
            skLineSegment(sketch, "E85", {"start": v(15, 120) * mm, "end": v(15, 108) * mm});
            skLineSegment(sketch, "E86", {"start": v(15, 108) * mm, "end": v(33, 90) * mm});
            skLineSegment(sketch, "E87", {"start": v(-80, 0) * mm, "end": v(80, 0) * mm, "construction": true});
            skLineSegment(sketch, "E88.MirrorCS", {"start": v(15, -108) * mm, "end": v(33, -90) * mm});
            skLineSegment(sketch, "E89.MirrorCS", {"start": v(15, -120) * mm, "end": v(15, -108) * mm});
            skArc(sketch, "E90.MirrorCS", {"start": v(-15, -120) * mm, "mid": v(0, -135) * mm, "end": v(15, -120) * mm});
            skLineSegment(sketch, "E91.MirrorCS", {"start": v(-15, -108) * mm, "end": v(-15, -120) * mm});
            skLineSegment(sketch, "E92.MirrorCS", {"start": v(-33, -90) * mm, "end": v(-15, -108) * mm});
            skCircle(sketch, "E93.MirrorC", {"center": v(0, -120) * mm, "radius": 6 * mm});
            skLineSegment(sketch, "E94.MirrorCS", {"start": v(0, -90) * mm, "end": v(0, -120) * mm, "construction": true});
            skSolve(sketch);
        }
        {
            var Q0;
            Q0 = qSketchRegion(id + "F16", true);
            var Q1;
            Q1=makeQuery(id+"F2.opExtrude","CAP_FACE",FACE,{"disambiguationData":[OSD([sQuery(id+"F0.wireOp",EDGE,"E12"),sQuery(id+"F0.wireOp",EDGE,"E13"),sQuery(id+"F0.wireOp",EDGE,"E14"),sQuery(id+"F0.wireOp",EDGE,"E15"),sQuery(id+"F0.wireOp",EDGE,"E17.filletArc"),sQuery(id+"F0.wireOp",EDGE,"E18.filletArc"),sQuery(id+"F0.wireOp",EDGE,"E19.filletArc"),sQuery(id+"F0.wireOp",EDGE,"E20.filletArc"),sQuery(id+"F0.wireOp",EDGE,"E25.0"),sQuery(id+"F0.wireOp",EDGE,"E25.1"),sQuery(id+"F0.wireOp",EDGE,"E25.2"),sQuery(id+"F0.wireOp",EDGE,"E25.3"),sQuery(id+"F0.wireOp",EDGE,"E25.4"),sQuery(id+"F0.wireOp",EDGE,"E25.5"),sQuery(id+"F0.wireOp",EDGE,"E25.6"),sQuery(id+"F0.wireOp",EDGE,"E25.7")])],"isStart":false});
            extrude(context, id + "F17", {"entities" : qUnion([Q0]), "endBound" : BoundingType.UP_TO_SURFACE, "endBoundEntityFace" : qUnion([Q1]), "depth" : 25 * mm});
        }
    });
